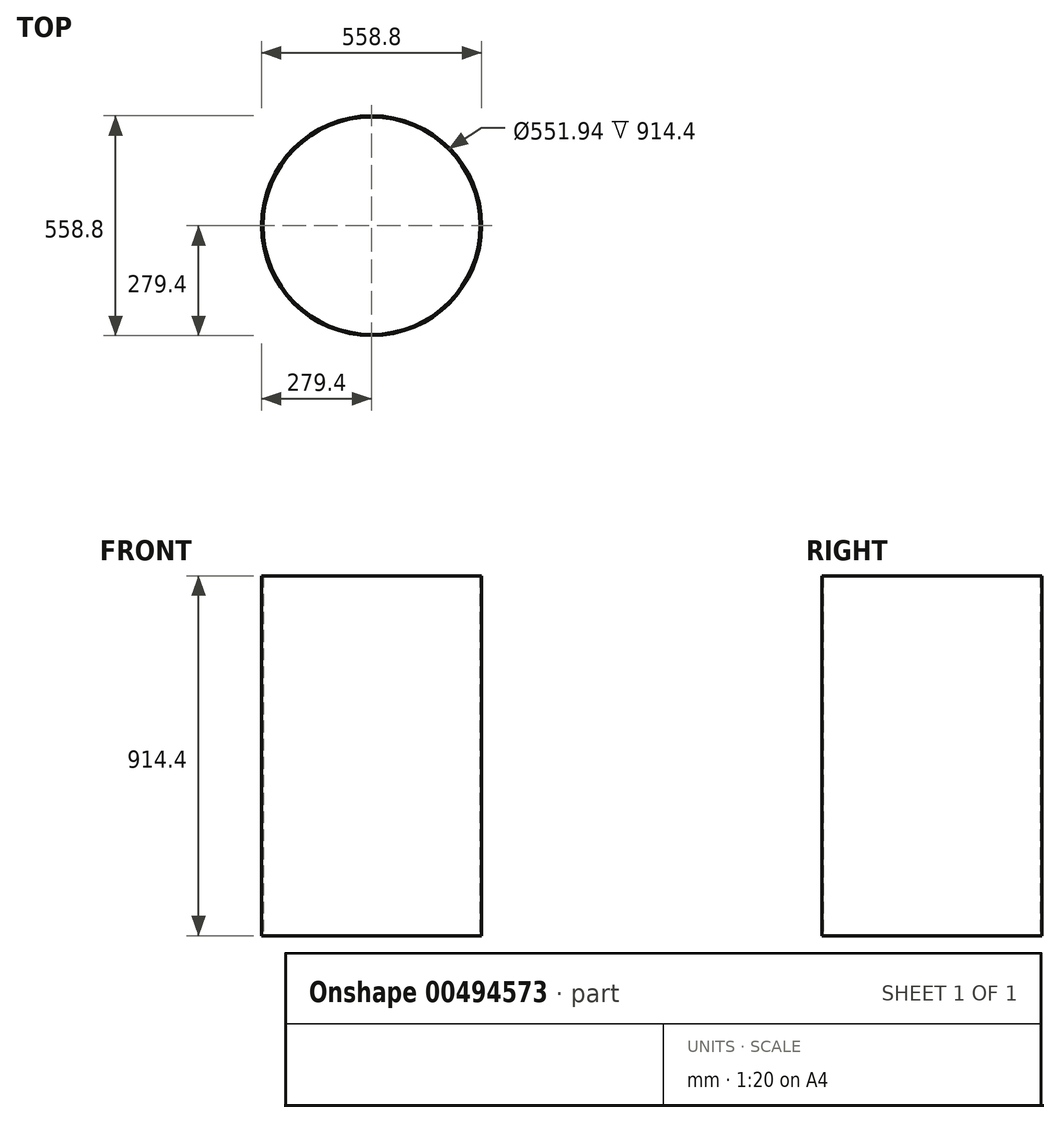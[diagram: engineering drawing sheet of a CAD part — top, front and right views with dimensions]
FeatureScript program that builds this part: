
annotation { "Feature Type Name" : "Feature", "Feature Type Description" : "" }
export const myFeature = defineFeature(function(context is Context, id is Id, definition is map)
    precondition{}
    {
        {
            var Q0;
            Q0=qCreatedBy(makeId("Top.planeOp"),FACE);
            var sketch = newSketch(context, id + "F0", { "sketchPlane" : qUnion([Q0])});
            skCircle(sketch, "E0", {"center": v(0, 0) * mm, "radius": 279.4 * mm});
            skCircle(sketch, "E1", {"center": v(0, 0) * mm, "radius": 275.97 * mm});
            skSolve(sketch);
        }
        {
            var Q0;
            Q0 = qSketchRegion(id + "F0", true);
            extrude(context, id + "F1", {"entities" : qUnion([Q0]), "depth" : 914.4 * mm});
        }
    });
